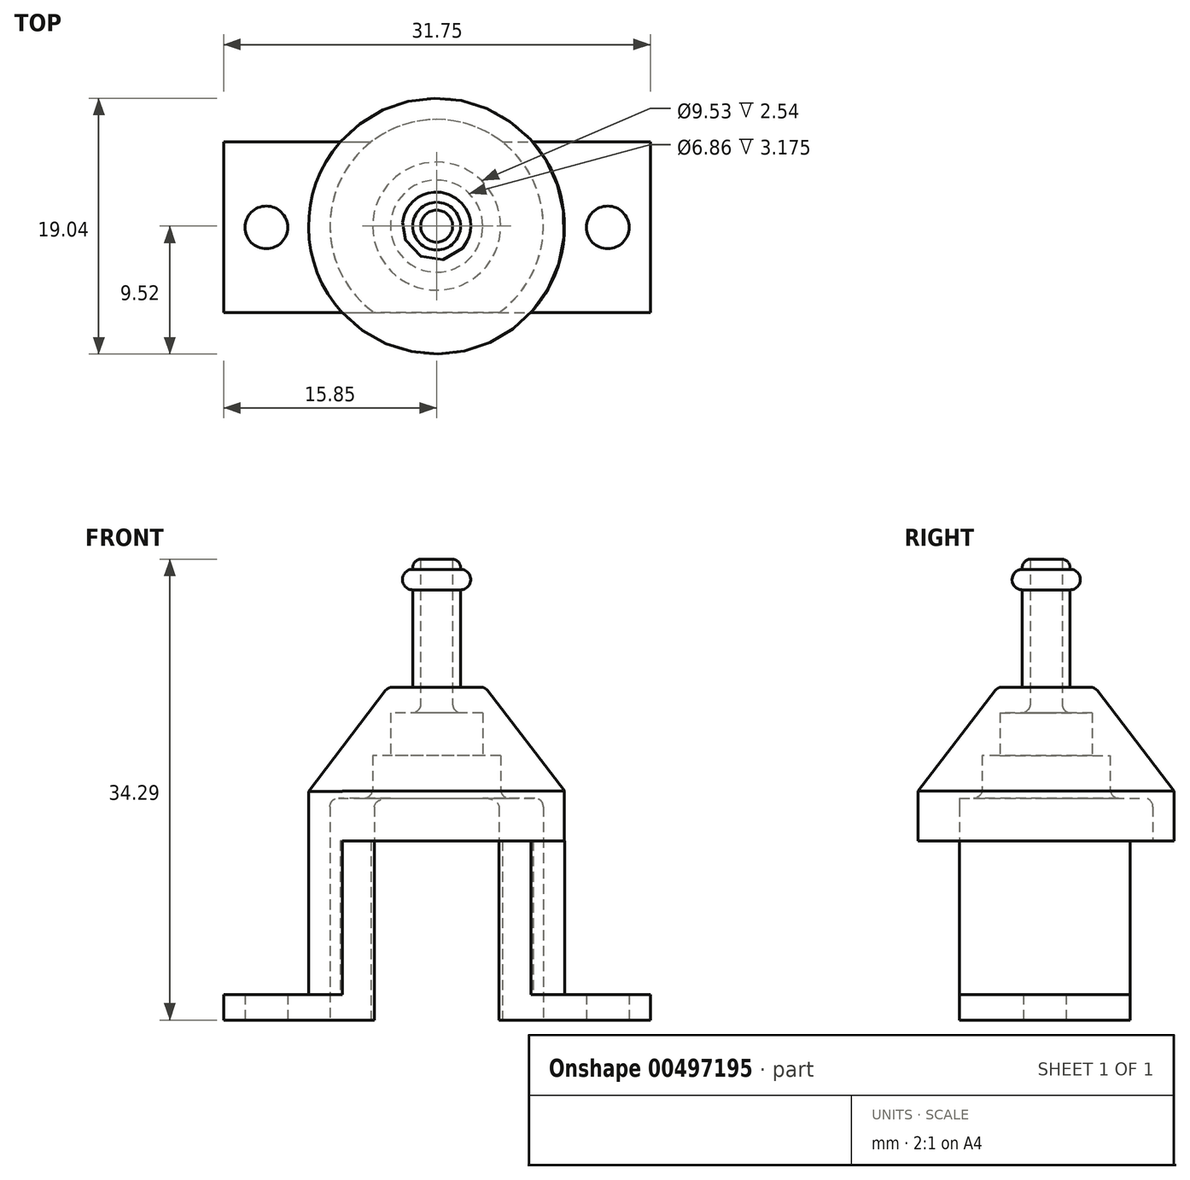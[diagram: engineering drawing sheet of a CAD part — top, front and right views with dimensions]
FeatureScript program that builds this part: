
annotation { "Feature Type Name" : "Feature", "Feature Type Description" : "" }
export const myFeature = defineFeature(function(context is Context, id is Id, definition is map)
    precondition{}
    {
        {
            var Q0;
            Q0=qCreatedBy(makeId("Top.planeOp"),FACE);
            var sketch = newSketch(context, id + "F0", { "sketchPlane" : qUnion([Q0])});
            skLineSegment(sketch, "E0.bottom", {"start": v(-15.85, 6.26) * mm, "end": v(15.9, 6.26) * mm});
            skLineSegment(sketch, "E0.top", {"start": v(-15.85, -6.44) * mm, "end": v(15.9, -6.44) * mm});
            skLineSegment(sketch, "E0.left", {"start": v(-15.85, 6.26) * mm, "end": v(-15.85, -6.44) * mm});
            skLineSegment(sketch, "E0.right", {"start": v(15.9, 6.26) * mm, "end": v(15.9, -6.44) * mm});
            skLineSegment(sketch, "E1", {"start": v(-15.85, -0.1) * mm, "end": v(15.9, -0.1) * mm, "construction": true});
            skCircle(sketch, "E2", {"center": v(-12.67, -0.1) * mm, "radius": 1.59 * mm, "construction": true});
            skLineSegment(sketch, "E3", {"start": v(0.03, -0.1) * mm, "end": v(0.03, 6.26) * mm, "construction": true});
            skCircle(sketch, "E4.MirrorC", {"center": v(12.73, -0.1) * mm, "radius": 1.59 * mm, "construction": true});
            skCircle(sketch, "E5.MirrorC", {"center": v(12.73, -0.1) * mm, "radius": 1.59 * mm});
            skCircle(sketch, "E6.MirrorC", {"center": v(-12.67, -0.1) * mm, "radius": 1.59 * mm});
            skSolve(sketch);
        }
        {
            var Q0;
            Q0=makeQuery(id+"F0.imprint","IMPRINT",FACE,{"disambiguationData":[TD([[makeQuery(id+"F0.imprint","IMPRINT",EDGE,{"derivedFrom":sQuery(id+"F0.wireOp",EDGE,"E0.bottom")}),-1.0]])]});
            extrude(context, id + "F1", {"entities" : qUnion([Q0]), "depth" : 1.9 * mm});
        }
        {
            var Q0;
            Q0=makeQuery(id+"F1.opExtrude","CAP_FACE",FACE,{"disambiguationData":[OSD([sQuery(id+"F0.wireOp",EDGE,"E0.bottom"),sQuery(id+"F0.wireOp",EDGE,"E0.top"),sQuery(id+"F0.wireOp",EDGE,"E0.left"),sQuery(id+"F0.wireOp",EDGE,"E0.right"),sQuery(id+"F0.wireOp",EDGE,"E5.MirrorC"),sQuery(id+"F0.wireOp",EDGE,"E6.MirrorC")])],"isStart":false});
            var sketch = newSketch(context, id + "F2", { "sketchPlane" : qUnion([Q0])});
            skArc(sketch, "E7", {"start": v(-4.89, 6.26) * mm, "mid": v(-7.94, -0.16) * mm, "end": v(-4.63, -6.44) * mm});
            skArc(sketch, "E8", {"start": v(-7.18, 6.26) * mm, "mid": v(-9.52, -0.13) * mm, "end": v(-7.01, -6.44) * mm});
            skLineSegment(sketch, "E9", {"start": v(-7.18, 6.26) * mm, "end": v(-4.89, 6.26) * mm});
            skLineSegment(sketch, "E10", {"start": v(-7.01, -6.44) * mm, "end": v(-4.63, -6.44) * mm});
            skLineSegment(sketch, "E11", {"start": v(7.18, 6.26) * mm, "end": v(4.89, 6.26) * mm});
            skLineSegment(sketch, "E12", {"start": v(7.01, -6.44) * mm, "end": v(4.63, -6.44) * mm});
            skArc(sketch, "E13.trimOffspring", {"start": v(7.01, -6.44) * mm, "mid": v(9.52, -0.13) * mm, "end": v(7.18, 6.26) * mm});
            skArc(sketch, "E14.trimOffspring", {"start": v(4.63, -6.44) * mm, "mid": v(7.94, -0.16) * mm, "end": v(4.89, 6.26) * mm});
            skSolve(sketch);
        }
        {
            var Q0;
            Q0=makeQuery(id+"F2.imprint","IMPRINT",FACE,{"disambiguationData":[TD([[makeQuery(id+"F2.imprint","IMPRINT",EDGE,{"derivedFrom":sQuery(id+"F2.wireOp",EDGE,"E7")}),-1.0]])]});
            var Q1;
            Q1=makeQuery(id+"F2.imprint","IMPRINT",FACE,{"disambiguationData":[TD([[makeQuery(id+"F2.imprint","IMPRINT",EDGE,{"derivedFrom":sQuery(id+"F2.wireOp",EDGE,"E11")}),-1.0]])]});
            extrude(context, id + "F3", {"entities" : qUnion([Q0, Q1]), "operationType" : NewBodyOperationType.ADD, "depth" : 11.43 * mm});
        }
        {
            var Q0;
            Q0=makeQuery(id+"F3.opExtrude","CAP_FACE",FACE,{"disambiguationData":[OSD([sQuery(id+"F2.wireOp",EDGE,"E7"),sQuery(id+"F2.wireOp",EDGE,"E8"),sQuery(id+"F2.wireOp",EDGE,"E9"),sQuery(id+"F2.wireOp",EDGE,"E10")])],"isStart":false});
            var sketch = newSketch(context, id + "F4", { "sketchPlane" : qUnion([Q0])});
            skCircle(sketch, "E15", {"center": v(0, 0) * mm, "radius": 9.52 * mm});
            skPoint(sketch, "E15.first.point", {"position": v(-7.01, -6.44) * mm});
            skPoint(sketch, "E15.second.point", {"position": v(-7.18, 6.26) * mm});
            skPoint(sketch, "E15.third.point", {"position": v(7, -6.44) * mm});
            skCircle(sketch, "E16", {"center": v(0, 0) * mm, "radius": 4.76 * mm});
            skLineSegment(sketch, "E17", {"start": v(-7.94, 0) * mm, "end": v(0, 0) * mm, "construction": true});
            skSolve(sketch);
        }
        {
            var Q0;
            Q0=makeQuery(id+"F4.imprint","IMPRINT",FACE,{"disambiguationData":[TD([[makeQuery(id+"F4.imprint","IMPRINT",EDGE,{"derivedFrom":makeQuery(id+"F3.opExtrude","CAP_EDGE",EDGE,{"disambiguationData":[OSD([sQuery(id+"F2.wireOp",EDGE,"E7")])],"isStart":false})}),-1.0]])]});
            var Q1;
            Q1=makeQuery(id+"F4.imprint","IMPRINT",FACE,{"disambiguationData":[TD([[makeQuery(id+"F4.imprint","IMPRINT",EDGE,{"derivedFrom":sQuery(id+"F4.wireOp",EDGE,"E16")}),-1.0]])]});
            extrude(context, id + "F5", {"entities" : qUnion([Q0, Q1]), "operationType" : NewBodyOperationType.ADD, "depth" : 6.35 * mm});
        }
        {
            var Q0;
            Q0=makeQuery(id+"F5.opExtrude","CAP_FACE",FACE,{"disambiguationData":[OSD([sQuery(id+"F2.wireOp",EDGE,"E8"),sQuery(id+"F4.wireOp",EDGE,"E15"),sQuery(id+"F4.wireOp",EDGE,"E16")])],"isStart":false});
            var sketch = newSketch(context, id + "F6", { "sketchPlane" : qUnion([Q0])});
            skLineSegment(sketch, "E18", {"start": v(-4.76, 0) * mm, "end": v(0, 0) * mm, "construction": true});
            skCircle(sketch, "E19", {"center": v(0, 0) * mm, "radius": 3.43 * mm});
            skCircle(sketch, "E20", {"center": v(0, 0) * mm, "radius": 8.9 * mm});
            skCircle(sketch, "E21", {"center": v(0, 0) * mm, "radius": 4.76 * mm});
            skSolve(sketch);
        }
        {
            var Q0;
            Q0=makeQuery(id+"F6.imprint","IMPRINT",FACE,{"disambiguationData":[TD([[makeQuery(id+"F6.imprint","IMPRINT",EDGE,{"derivedFrom":sQuery(id+"F6.wireOp",EDGE,"E20")}),1.0]])]});
            var Q1;
            Q1=makeQuery(id+"F6.imprint","IMPRINT",FACE,{"disambiguationData":[TD([[makeQuery(id+"F6.imprint","IMPRINT",EDGE,{"derivedFrom":sQuery(id+"F6.wireOp",EDGE,"E19")}),-1.0]])]});
            var Q2;
            Q2=sQuery(id+"F6.wireOp",EDGE,"ZektFupa-XtR3-63pd-Dniz-zUc07Kjgoyrp");
            var Q3;
            Q3=sQuery(id+"F6.wireOp",EDGE,"48pFREp7-2D9j-I25v-mjOP-Yk5lB4QPco76");
            extrude(context, id + "F7", {"entities" : qUnion([Q0, Q1]), "operationType" : NewBodyOperationType.ADD, "surfaceEntities" : qUnion([Q2, Q3]), "depth" : 3.17 * mm});
        }
        {
            var Q0;
            Q0=makeQuery(id+"F7.opExtrude","CAP_FACE",FACE,{"disambiguationData":[OSD([sQuery(id+"F6.wireOp",EDGE,"E19"),sQuery(id+"F6.wireOp",EDGE,"E20")])],"isStart":false});
            var sketch = newSketch(context, id + "F8", { "sketchPlane" : qUnion([Q0])});
            skLineSegment(sketch, "E22", {"start": v(-3.43, 0) * mm, "end": v(0, 0) * mm, "construction": true});
            skCircle(sketch, "E23", {"center": v(0, 0) * mm, "radius": 1.2 * mm});
            skCircle(sketch, "E24", {"center": v(0, 0) * mm, "radius": 4.76 * mm});
            skCircle(sketch, "E25", {"center": v(0, 0) * mm, "radius": 6.5 * mm});
            skSolve(sketch);
        }
        {
            var Q0;
            Q0=makeQuery(id+"F8.imprint","IMPRINT",FACE,{"disambiguationData":[TD([[makeQuery(id+"F8.imprint","IMPRINT",EDGE,{"derivedFrom":sQuery(id+"F8.wireOp",EDGE,"E24")}),1.0]])]});
            var Q1;
            Q1=makeQuery(id+"F8.imprint","IMPRINT",FACE,{"disambiguationData":[TD([[makeQuery(id+"F8.imprint","IMPRINT",EDGE,{"derivedFrom":sQuery(id+"F8.wireOp",EDGE,"E23")}),-1.0]])]});
            var Q2;
            Q2=makeQuery(id+"F8.imprint","IMPRINT",FACE,{"disambiguationData":[TD([[makeQuery(id+"F8.imprint","IMPRINT",EDGE,{"derivedFrom":sQuery(id+"F8.wireOp",EDGE,"E24")}),-1.0]])]});
            extrude(context, id + "F9", {"entities" : qUnion([Q0, Q1, Q2]), "operationType" : NewBodyOperationType.ADD, "depth" : 1.9 * mm});
        }
        {
            var Q0;
            Q0=makeQuery(id+"F9.opExtrude","CAP_FACE",FACE,{"disambiguationData":[OSD([sQuery(id+"F8.wireOp",EDGE,"E23"),sQuery(id+"F8.wireOp",EDGE,"E24")])],"isStart":false});
            var sketch = newSketch(context, id + "F10", { "sketchPlane" : qUnion([Q0])});
            skLineSegment(sketch, "E26", {"start": v(-1.2, 0) * mm, "end": v(0, 0) * mm, "construction": true});
            skCircle(sketch, "E27", {"center": v(0, 0) * mm, "radius": 1.78 * mm});
            skSolve(sketch);
        }
        {
            var Q0;
            Q0=makeQuery(id+"F10.imprint","IMPRINT",FACE,{"disambiguationData":[TD([[makeQuery(id+"F10.imprint","IMPRINT",EDGE,{"derivedFrom":sQuery(id+"F10.wireOp",EDGE,"E27")}),1.0]])]});
            extrude(context, id + "F11", {"entities" : qUnion([Q0]), "operationType" : NewBodyOperationType.ADD, "depth" : 9.52 * mm});
        }
        {
            var Q0;
            Q0=qCreatedBy(makeId("Front.planeOp"),FACE);
            var sketch = newSketch(context, id + "F12", { "sketchPlane" : qUnion([Q0])});
            skLineSegment(sketch, "E28", {"start": v(0, 43.84) * mm, "end": v(0, 33.53) * mm, "construction": true});
            skLineSegment(sketch, "E29", {"start": v(0, 33.53) * mm, "end": v(-1.78, 33.53) * mm});
            skLineSegment(sketch, "E30", {"start": v(-1.78, 33.53) * mm, "end": v(-1.78, 32) * mm});
            skArc(sketch, "E31", {"start": v(-1.78, 33.53) * mm, "mid": v(-2.54, 32.77) * mm, "end": v(-1.78, 32) * mm});
            skSolve(sketch);
        }
        {
            var Q0;
            Q0=makeQuery(id+"F12.imprint","IMPRINT",FACE,{"disambiguationData":[TD([[makeQuery(id+"F12.imprint","IMPRINT",EDGE,{"derivedFrom":sQuery(id+"F12.wireOp",EDGE,"E30")}),-1.0]])]});
            var Q1;
            Q1=sQuery(id+"F12.wireOp",EDGE,"E28");
            revolve(context, id + "F13", {"operationType" : NewBodyOperationType.ADD, "entities" : qUnion([Q0]), "axis" : qUnion([Q1]), "revolveType" : RevolveType.FULL});
        }
        {
            var Q0;
            Q0=qCreatedBy(makeId("Front.planeOp"),FACE);
            var sketch = newSketch(context, id + "F14", { "sketchPlane" : qUnion([Q0])});
            skLineSegment(sketch, "E32", {"start": v(0, 24.83) * mm, "end": v(0, 17.02) * mm});
            skLineSegment(sketch, "E33", {"start": v(0, 17.02) * mm, "end": v(-9.53, 17.02) * mm});
            skLineSegment(sketch, "E34", {"start": v(-9.53, 17.02) * mm, "end": v(-3.56, 24.83) * mm});
            skLineSegment(sketch, "E35", {"start": v(-3.56, 24.83) * mm, "end": v(0, 24.83) * mm});
            skLineSegment(sketch, "E36", {"start": v(-9.53, 17.02) * mm, "end": v(-9.53, 24.8) * mm});
            skLineSegment(sketch, "E37", {"start": v(-9.53, 24.8) * mm, "end": v(-6.97, 24.8) * mm});
            skLineSegment(sketch, "E38", {"start": v(-6.97, 24.8) * mm, "end": v(-3.56, 24.83) * mm});
            skSolve(sketch);
        }
        {
            var Q0;
            Q0=makeQuery(id+"F14.imprint","IMPRINT",FACE,{"disambiguationData":[TD([[makeQuery(id+"F14.imprint","IMPRINT",EDGE,{"derivedFrom":sQuery(id+"F14.wireOp",EDGE,"E34")}),1.0]])]});
            var Q1;
            Q1=sQuery(id+"F14.wireOp",EDGE,"E32");
            revolve(context, id + "F15", {"operationType" : NewBodyOperationType.REMOVE, "entities" : qUnion([Q0]), "axis" : qUnion([Q1]), "revolveType" : RevolveType.FULL, "oppositeDirection" : true});
        }
        {
            var Q0;
            Q0=makeQuery(id+"F1.opExtrude","CAP_FACE",FACE,{"disambiguationData":[OSD([sQuery(id+"F0.wireOp",EDGE,"E0.bottom"),sQuery(id+"F0.wireOp",EDGE,"E0.top"),sQuery(id+"F0.wireOp",EDGE,"E0.left"),sQuery(id+"F0.wireOp",EDGE,"E0.right"),sQuery(id+"F0.wireOp",EDGE,"E5.MirrorC"),sQuery(id+"F0.wireOp",EDGE,"E6.MirrorC")])],"isStart":true});
            var sketch = newSketch(context, id + "F16", { "sketchPlane" : qUnion([Q0])});
            skArc(sketch, "E39", {"start": v(-4.63, 6.44) * mm, "mid": v(0, -7.94) * mm, "end": v(4.63, 6.44) * mm});
            skLineSegment(sketch, "E40", {"start": v(-4.63, 6.44) * mm, "end": v(4.63, 6.44) * mm});
            skLineSegment(sketch, "E41", {"start": v(-4.89, -6.26) * mm, "end": v(4.89, -6.26) * mm});
            skSolve(sketch);
        }
        {
            var Q0;
            Q0 = qSketchRegion(id + "F16", true);
            extrude(context, id + "F17", {"entities" : qUnion([Q0]), "operationType" : NewBodyOperationType.REMOVE, "oppositeDirection" : true, "depth" : 16.5 * mm});
        }
        {
            var Q0;
            Q0=makeQuery(id+"F15.boolean.opBoolean","INTERSECT",EDGE,{"derivedFrom":[makeQuery(id+"F9.opExtrude","CAP_FACE",FACE,{"disambiguationData":[OSD([sQuery(id+"F8.wireOp",EDGE,"E23"),sQuery(id+"F8.wireOp",EDGE,"E24")])],"isStart":false}),makeQuery(id+"F15.opRevolve","SWEPT_FACE",FACE,{"disambiguationData":[OSD([sQuery(id+"F14.wireOp",EDGE,"E34")])]})]});
            var Q1;
            Q1=makeQuery(id+"F3.opExtrude","CAP_EDGE",EDGE,{"disambiguationData":[OSD([sQuery(id+"F2.wireOp",EDGE,"E13.trimOffspring")])],"isStart":true});
            var Q2;
            Q2=makeQuery(id+"F11.opExtrude","CAP_EDGE",EDGE,{"disambiguationData":[OSD([sQuery(id+"F10.wireOp",EDGE,"E27")])],"isStart":false});
            var Q3;
            Q3=makeQuery(id+"F3.opExtrude","CAP_EDGE",EDGE,{"disambiguationData":[OSD([sQuery(id+"F2.wireOp",EDGE,"E8")])],"isStart":true});
            var Q4;
            Q4=makeQuery(id+"F17.boolean.opBoolean","COPY",EDGE,{"disambiguationData":[OD(0.0)],"derivedFrom":makeQuery(id+"F17.opExtrude","CAP_EDGE",EDGE,{"disambiguationData":[OSD([sQuery(id+"F16.wireOp",EDGE,"E39")])],"isStart":true})});
            var Q5;
            Q5=makeQuery(id+"F17.boolean.opBoolean","COPY",EDGE,{"disambiguationData":[OD(1.0)],"derivedFrom":makeQuery(id+"F17.opExtrude","CAP_EDGE",EDGE,{"disambiguationData":[OSD([sQuery(id+"F16.wireOp",EDGE,"E39")])],"isStart":true})});
            var Q6;
            Q6=makeQuery(id+"F17.boolean.opBoolean","INTERSECT",EDGE,{"derivedFrom":[makeQuery(id+"F5.opExtrude","SWEPT_FACE",FACE,{"disambiguationData":[OSD([sQuery(id+"F4.wireOp",EDGE,"E16")])]}),makeQuery(id+"F17.opExtrude","CAP_FACE",FACE,{"disambiguationData":[OSD([sQuery(id+"F16.wireOp",EDGE,"E39"),sQuery(id+"F16.wireOp",EDGE,"E40")])],"isStart":false})]});
            var Q7;
            Q7=makeQuery(id+"F7.opExtrude","CAP_EDGE",EDGE,{"disambiguationData":[OSD([sQuery(id+"F6.wireOp",EDGE,"ZektFupa-XtR3-63pd-Dniz-zUc07Kjgoyrp")])],"isStart":true});
            var Q8;
            Q8=makeQuery(id+"F9.opExtrude","CAP_EDGE",EDGE,{"disambiguationData":[OSD([sQuery(id+"F8.wireOp",EDGE,"E23")])],"isStart":true});
            var Q9;
            Q9=makeQuery(id+"F17.boolean.opBoolean","COPY",EDGE,{"derivedFrom":makeQuery(id+"F17.opExtrude","CAP_EDGE",EDGE,{"disambiguationData":[OSD([sQuery(id+"F16.wireOp",EDGE,"E39")])],"isStart":false})});
            var Q10;
            Q10=makeQuery(id+"F5.opExtrude","CAP_EDGE",EDGE,{"disambiguationData":[OSD([sQuery(id+"F4.wireOp",EDGE,"E16")])],"isStart":false});
            var Q11;
            Q11=makeQuery(id+"F7.opExtrude","CAP_EDGE",EDGE,{"disambiguationData":[OSD([sQuery(id+"F6.wireOp",EDGE,"ZektFupa-XtR3-63pd-Dniz-zUc07Kjgoyrp")])],"isStart":false});
            fillet(context, id + "F18", {"entities" : qUnion([Q0, Q1, Q2, Q3, Q4, Q5, Q6, Q7, Q8, Q9, Q10, Q11]), "radius" : 0.64 * mm, "tangentPropagation" : true, "allowEdgeOverflow" : false});
        }
    });
